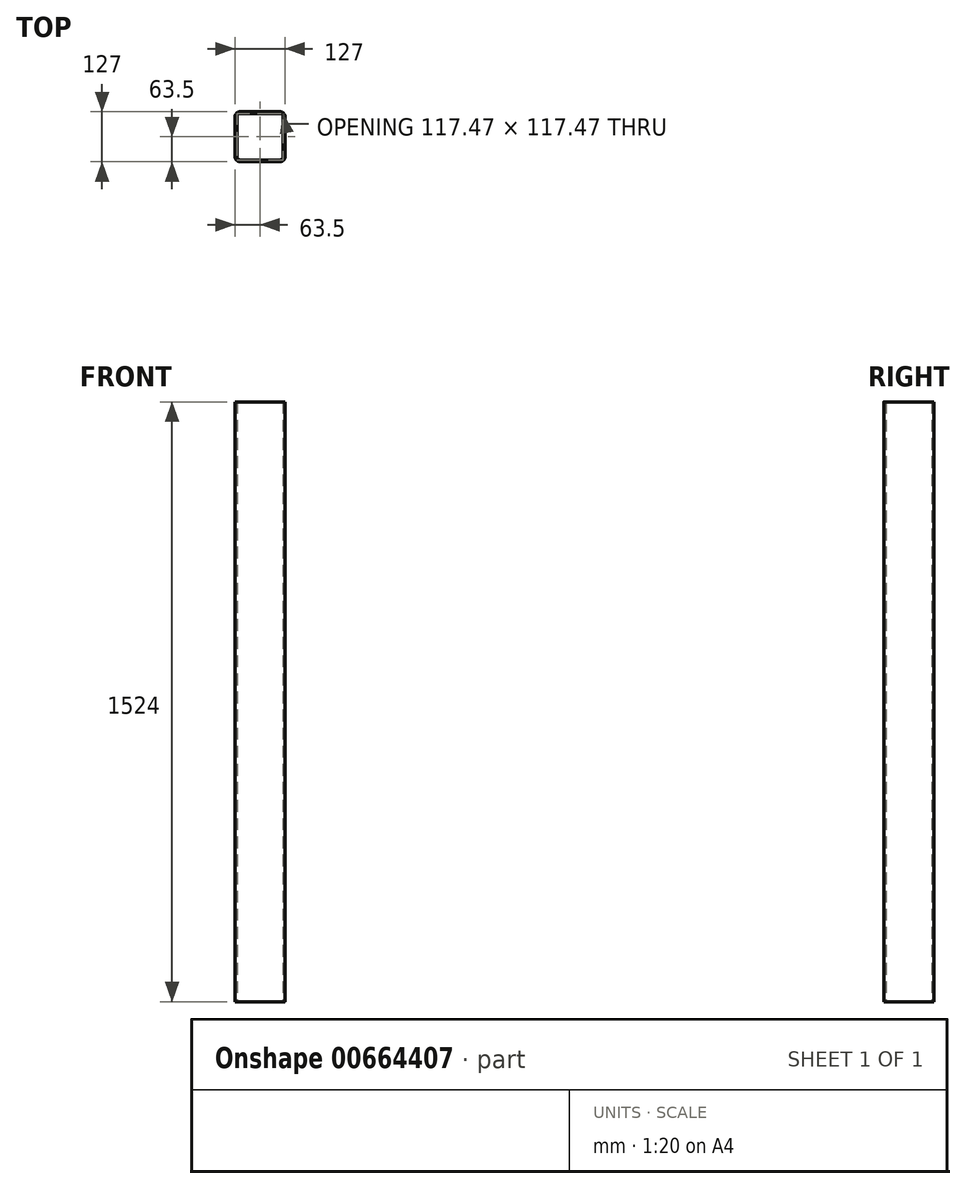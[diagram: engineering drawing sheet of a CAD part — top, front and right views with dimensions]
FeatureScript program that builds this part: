
annotation { "Feature Type Name" : "Feature", "Feature Type Description" : "" }
export const myFeature = defineFeature(function(context is Context, id is Id, definition is map)
    precondition{}
    {
        {
            var Q0;
            Q0=qCreatedBy(makeId("Top.planeOp"),FACE);
            var sketch = newSketch(context, id + "F0", { "sketchPlane" : qUnion([Q0])});
            skLineSegment(sketch, "E0.bottom", {"start": v(50.8, -63.5) * mm, "end": v(-50.8, -63.5) * mm});
            skLineSegment(sketch, "E0.top", {"start": v(50.8, 63.5) * mm, "end": v(-50.8, 63.5) * mm});
            skLineSegment(sketch, "E0.left", {"start": v(63.5, -50.8) * mm, "end": v(63.5, 50.8) * mm});
            skLineSegment(sketch, "E0.right", {"start": v(-63.5, -50.8) * mm, "end": v(-63.5, 50.8) * mm});
            skPoint(sketch, "E0.middle", {"position": v(0, 0) * mm});
            skPoint(sketch, "E1.visualSharp", {"position": v(-63.5, 63.5) * mm});
            skArc(sketch, "E1.filletArc", {"start": v(-50.8, 63.5) * mm, "mid": v(-59.78, 59.78) * mm, "end": v(-63.5, 50.8) * mm});
            skPoint(sketch, "E2.visualSharp", {"position": v(63.5, 63.5) * mm});
            skArc(sketch, "E2.filletArc", {"start": v(63.5, 50.8) * mm, "mid": v(59.78, 59.78) * mm, "end": v(50.8, 63.5) * mm});
            skPoint(sketch, "E3.visualSharp", {"position": v(63.5, -63.5) * mm});
            skArc(sketch, "E3.filletArc", {"start": v(50.8, -63.5) * mm, "mid": v(59.78, -59.78) * mm, "end": v(63.5, -50.8) * mm});
            skPoint(sketch, "E4.visualSharp", {"position": v(-63.5, -63.5) * mm});
            skArc(sketch, "E4.filletArc", {"start": v(-63.5, -50.8) * mm, "mid": v(-59.78, -59.78) * mm, "end": v(-50.8, -63.5) * mm});
            skArc(sketch, "E5.0", {"start": v(58.74, 50.8) * mm, "mid": v(56.41, 56.41) * mm, "end": v(50.8, 58.74) * mm});
            skLineSegment(sketch, "E5.1", {"start": v(58.74, -50.8) * mm, "end": v(58.74, 50.8) * mm});
            skLineSegment(sketch, "E5.2", {"start": v(50.8, 58.74) * mm, "end": v(-50.8, 58.74) * mm});
            skArc(sketch, "E5.3", {"start": v(50.8, -58.74) * mm, "mid": v(56.41, -56.41) * mm, "end": v(58.74, -50.8) * mm});
            skArc(sketch, "E5.4", {"start": v(-50.8, 58.74) * mm, "mid": v(-56.41, 56.41) * mm, "end": v(-58.74, 50.8) * mm});
            skLineSegment(sketch, "E5.5", {"start": v(-58.74, -50.8) * mm, "end": v(-58.74, 50.8) * mm});
            skArc(sketch, "E5.6", {"start": v(-58.74, -50.8) * mm, "mid": v(-56.41, -56.41) * mm, "end": v(-50.8, -58.74) * mm});
            skLineSegment(sketch, "E5.7", {"start": v(50.8, -58.74) * mm, "end": v(-50.8, -58.74) * mm});
            skSolve(sketch);
        }
        {
            var Q0;
            Q0 = qSketchRegion(id + "F0", true);
            extrude(context, id + "F1", {"entities" : qUnion([Q0]), "depth" : 1524 * mm, "offsetDistance" : 25.4 * mm});
        }
    });
